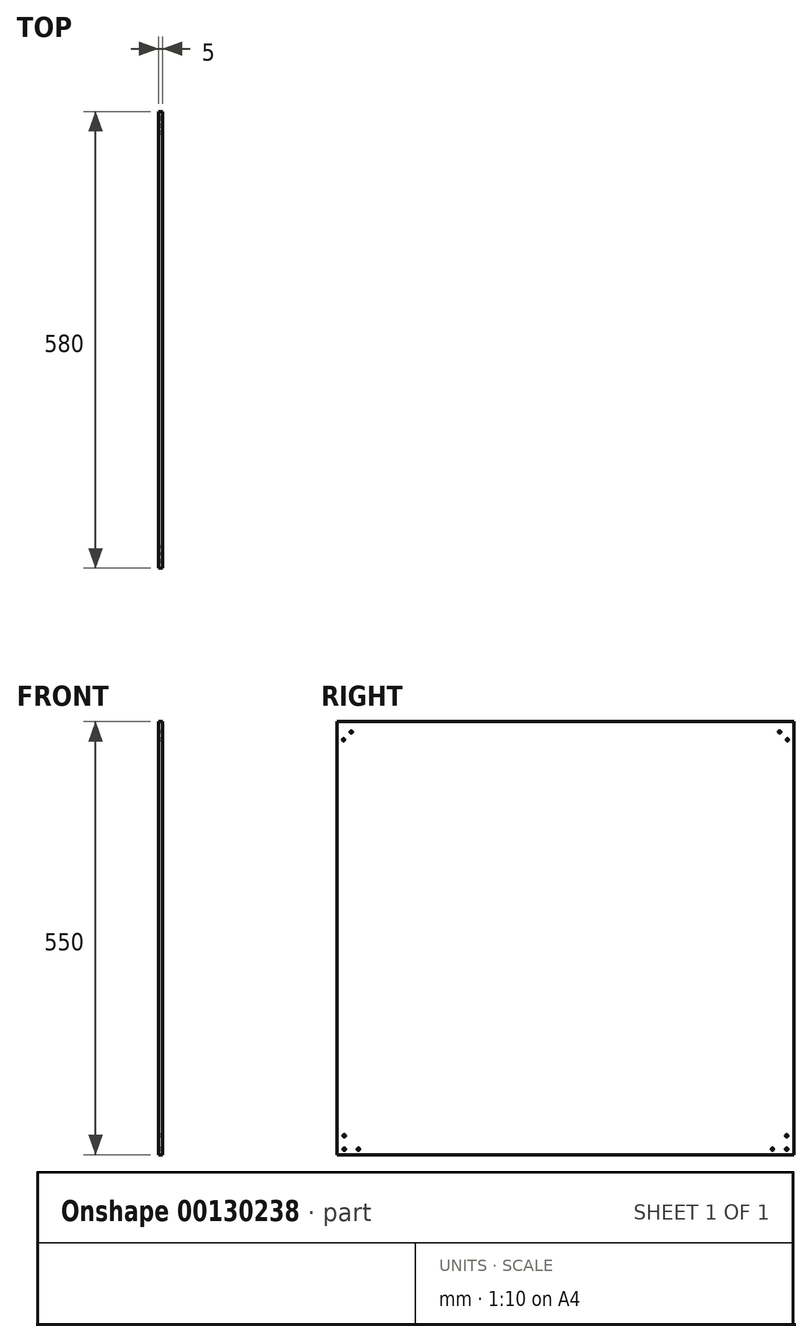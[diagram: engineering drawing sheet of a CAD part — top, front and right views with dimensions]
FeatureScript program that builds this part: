
annotation { "Feature Type Name" : "Feature", "Feature Type Description" : "" }
export const myFeature = defineFeature(function(context is Context, id is Id, definition is map)
    precondition{}
    {
        {
            var Q0;
            Q0=qCreatedBy(makeId("Right.planeOp"),FACE);
            var sketch = newSketch(context, id + "F0", { "sketchPlane" : qUnion([Q0])});
            skLineSegment(sketch, "E0.bottom", {"start": v(290, 275) * mm, "end": v(-290, 275) * mm});
            skLineSegment(sketch, "E0.top", {"start": v(290, -275) * mm, "end": v(-290, -275) * mm});
            skLineSegment(sketch, "E0.left", {"start": v(290, 275) * mm, "end": v(290, -275) * mm});
            skLineSegment(sketch, "E0.right", {"start": v(-290, 275) * mm, "end": v(-290, -275) * mm});
            skPoint(sketch, "E0.middle", {"position": v(0, 0) * mm});
            skCircle(sketch, "E1", {"center": v(-281, -251) * mm, "radius": 1.5 * mm});
            skCircle(sketch, "E2", {"center": v(-263, -268.03) * mm, "radius": 1.5 * mm});
            skCircle(sketch, "E3", {"center": v(-281, -268) * mm, "radius": 1.5 * mm});
            skCircle(sketch, "E4.MirrorC", {"center": v(263, -268.03) * mm, "radius": 1.5 * mm});
            skCircle(sketch, "E5.MirrorC", {"center": v(281, -268) * mm, "radius": 1.5 * mm});
            skCircle(sketch, "E6.MirrorC", {"center": v(281, -251) * mm, "radius": 1.5 * mm});
            skCircle(sketch, "E7", {"center": v(-272, 262) * mm, "radius": 1.5 * mm});
            skCircle(sketch, "E8", {"center": v(-282, 252) * mm, "radius": 1.5 * mm});
            skCircle(sketch, "E9.MirrorC", {"center": v(282, 252) * mm, "radius": 1.5 * mm});
            skCircle(sketch, "E10.MirrorC", {"center": v(272, 262) * mm, "radius": 1.5 * mm});
            skSolve(sketch);
        }
        {
            var Q0;
            Q0=makeQuery(id+"F0.imprint","IMPRINT",FACE,{"disambiguationData":[TD([[makeQuery(id+"F0.imprint","IMPRINT",EDGE,{"derivedFrom":sQuery(id+"F0.wireOp",EDGE,"E0.bottom")}),1.0]])]});
            extrude(context, id + "F1", {"entities" : qUnion([Q0]), "endBound" : BoundingType.SYMMETRIC, "depth" : 5 * mm});
        }
    });
